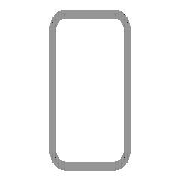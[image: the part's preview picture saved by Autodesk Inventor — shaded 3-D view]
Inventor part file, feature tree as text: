
AUTODESK INVENTOR PART (.ipt)
format: ipt  version: 2025.1 (Build 291241020, 241B)  size: 134,144 bytes
history: native  units: mm (DEFAULTED — no unit token found)
features: other x4, sketch x1, plane x1
ambient origin geometry x8: Origin, YZ Plane, XZ Plane, XY Plane, X Axis, Y Axis, Z Axis, Center Point
bodies: Solid1 (feature_tree), Body (feature_tree)
feature tree (6):
  parser-record x1  (decoder bookkeeping rows leaked as tree rows — omitted from the tree; the rows remain in map.json)
  other  "Driven Length"
  other  "Start Plane"
  other  "End Plane"
  sketch  "Sketch3"  dims[d3=580.0mm d4=0.0mm d7=4.0mm d9=20.0mm d11=40.0mm d12=2.0mm d13=20.0mm d14=600.0mm d15=10.0mm d16=20.0mm d17=90.0deg d18=580.0mm]
  plane  "Work Plane3"
